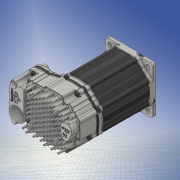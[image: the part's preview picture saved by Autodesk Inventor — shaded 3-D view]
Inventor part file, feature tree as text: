
AUTODESK INVENTOR PART (.ipt)
format: ipt  version: 2016 (Build 200138000, 138)  size: 17,383,424 bytes
history: native  units: in
note: dims shown in document units (in); Inventor stores cm internally (conversion verified against a paired STEP export)
features: other x21, extrude x1
ambient origin geometry x8: Origin, YZ Plane, XZ Plane, XY Plane, X Axis, Y Axis, Z Axis, Center Point
bodies: Solid1 (feature_tree), Solid2 (feature_tree), Solid3 (feature_tree), Solid4 (feature_tree), Solid5 (feature_tree), Solid6 (feature_tree), Solid7 (feature_tree), Solid8 (feature_tree), Solid9 (feature_tree), Solid10 (feature_tree), Solid11 (feature_tree), Solid12 (feature_tree), Solid13 (feature_tree), Solid14 (feature_tree), Solid15 (feature_tree), Solid16 (feature_tree), Solid17 (feature_tree), Solid18 (feature_tree), Solid19 (feature_tree), Solid20 (feature_tree)
feature tree (22):
  other  "shaft 23xx_customer-1-solid1"
  other  "end bell front  M23xx_customer-1-solid1"
  other  "1106822 end plate 23xx CP_customer-1-solid1"
  other  "1106824 gasket 23xx CP_customer-1-solid1"
  other  "1106887-1-solid1"
  other  "1106823 cover 23xx CP_customer-1-solid1"
  other  "1104396 4-40 x  .5 threadformer-1-solid1"
  other  "1104396 4-40 x  .5 threadformer-2-solid1"
  other  "1104396 4-40 x  .5 threadformer-3-solid1"
  other  "1104396 4-40 x  .5 threadformer-4-solid1"
  other  "1104396 4-40 x  .5 threadformer-5-solid1"
  other  "1104396 4-40 x  .5 threadformer-6-solid1"
  other  "1104396 4-40 x  .5 threadformer-7-solid1"
  other  "1104396 4-40 x  .5 threadformer-8-solid1"
  other  "1104396 4-40 x  .5 threadformer-9-solid1"
  other  "1104396 4-40 x  .5 threadformer-10-solid1"
  other  "1104396 4-40 x  .5 threadformer-11-solid1"
  other  "1104396 4-40 x  .5 threadformer-12-solid1"
  extrude  "extrusion 23xx_customer-1-solid1"  [1 undecoded]
  other  "4pin minifit-2-solid1"
  other  "8 pin minifit-1-surface1"
  other  "Srf1"
note: 1 required parameter value undecoded (feature->parameter linkage not recoverable at this tier; creation-order binding heuristic only, values carry confidence <= 0.55)
